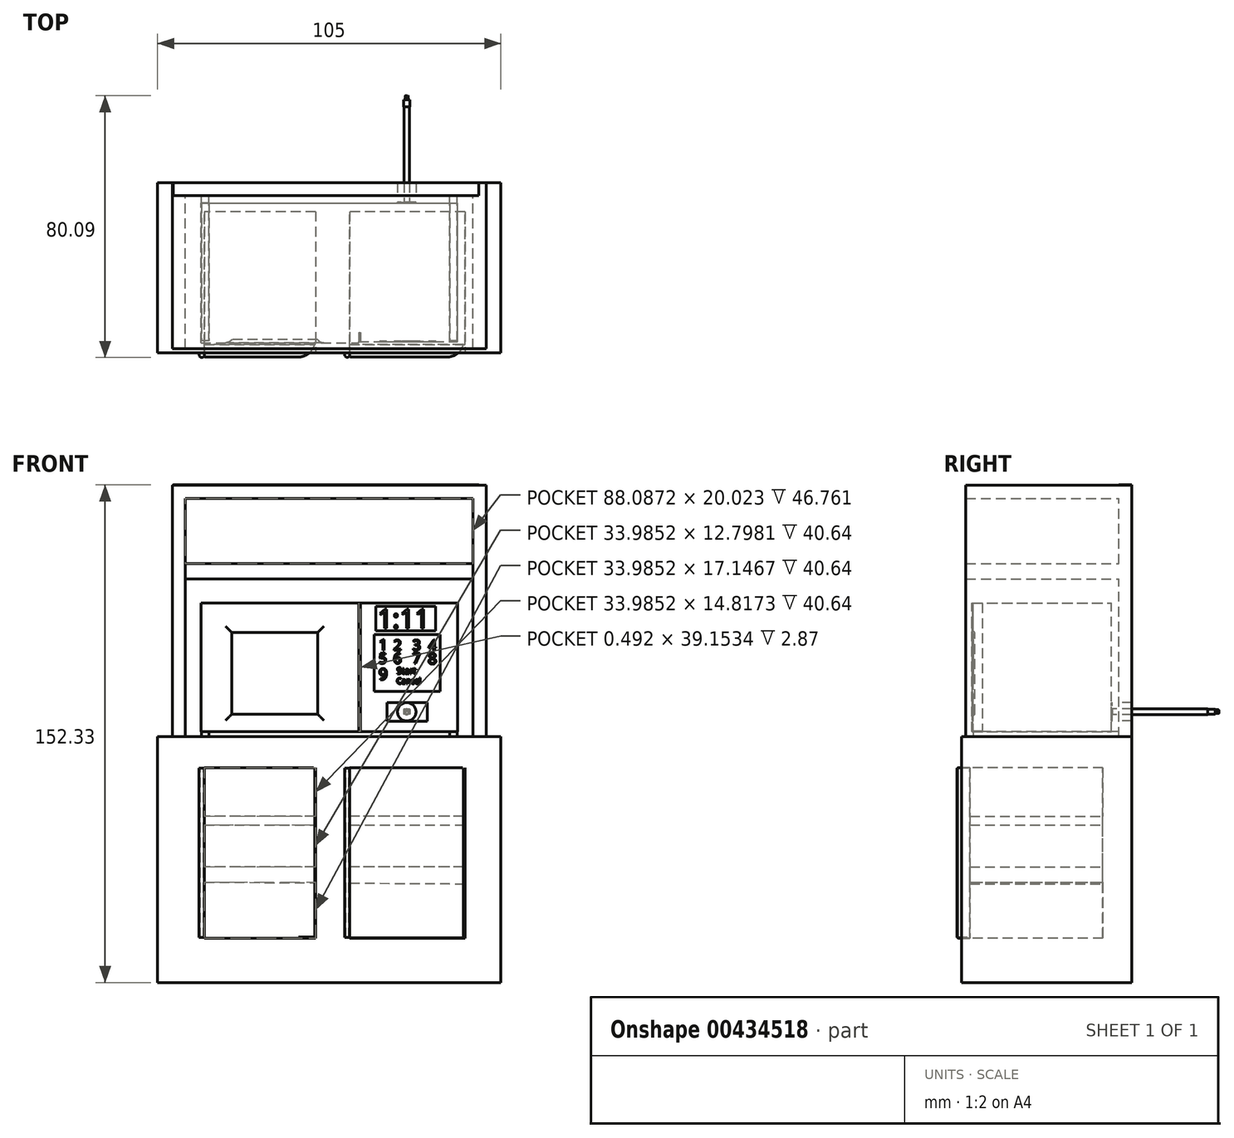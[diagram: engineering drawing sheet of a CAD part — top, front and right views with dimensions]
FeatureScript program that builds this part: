
annotation { "Feature Type Name" : "Feature", "Feature Type Description" : "" }
export const myFeature = defineFeature(function(context is Context, id is Id, definition is map)
    precondition{}
    {
        {
            var Q0;
            Q0=qCreatedBy(makeId("Front.planeOp"),FACE);
            var sketch = newSketch(context, id + "F0", { "sketchPlane" : qUnion([Q0])});
            skLineSegment(sketch, "E0", {"start": v(-38.7, 76.96) * mm, "end": v(57.3, 76.96) * mm});
            skLineSegment(sketch, "E1", {"start": v(57.3, 76.96) * mm, "end": v(57.3, 0) * mm});
            skLineSegment(sketch, "E2", {"start": v(53.34, 0) * mm, "end": v(53.34, 73) * mm});
            skLineSegment(sketch, "E3", {"start": v(53.34, 73) * mm, "end": v(-34.75, 73) * mm});
            skLineSegment(sketch, "E4", {"start": v(-34.75, 73) * mm, "end": v(-34.75, 0) * mm});
            skLineSegment(sketch, "E5", {"start": v(-38.7, 0) * mm, "end": v(-38.7, 76.96) * mm});
            skLineSegment(sketch, "E6", {"start": v(61.8, 0) * mm, "end": v(-43.2, 0) * mm});
            skLineSegment(sketch, "E7", {"start": v(-43.2, 0) * mm, "end": v(-43.2, -75.21) * mm});
            skLineSegment(sketch, "E8", {"start": v(-43.2, -75.21) * mm, "end": v(61.8, -75.21) * mm});
            skLineSegment(sketch, "E9", {"start": v(61.8, -75.21) * mm, "end": v(61.8, 0) * mm});
            skSolve(sketch);
        }
        {
            var Q0;
            Q0=makeQuery(id+"F0.imprint","IMPRINT",FACE,{"disambiguationData":[TD([[makeQuery(id+"F0.imprint","IMPRINT",EDGE,{"derivedFrom":sQuery(id+"F0.wireOp",EDGE,"E0")}),-1.0]])]});
            extrude(context, id + "F1", {"entities" : qUnion([Q0]), "depth" : 50.8 * mm});
        }
        {
            var Q0;
            {var subQ6=sQuery(id+"F0.wireOp",EDGE,"E7");Q0=makeQuery(id+"F0.imprint","IMPRINT",FACE,{"disambiguationData":[TD([[makeQuery(id+"F0.imprint","IMPRINT",EDGE,{"derivedFrom":subQ6}),1.0]])]});}
            extrude(context, id + "F2", {"entities" : qUnion([Q0]), "operationType" : NewBodyOperationType.ADD, "depth" : 52.07 * mm});
        }
        {
            var Q0;
            Q0=qCreatedBy(makeId("Right.planeOp"),FACE);
            var sketch = newSketch(context, id + "F3", { "sketchPlane" : qUnion([Q0])});
            skLineSegment(sketch, "E10", {"start": v(0, 77.12) * mm, "end": v(0, 0) * mm});
            skLineSegment(sketch, "E11", {"start": v(0, 0) * mm, "end": v(-3.98, 0) * mm});
            skLineSegment(sketch, "E12", {"start": v(-3.98, 0) * mm, "end": v(-3.98, 77.12) * mm});
            skLineSegment(sketch, "E13", {"start": v(-3.98, 77.12) * mm, "end": v(0, 77.12) * mm});
            skSolve(sketch);
        }
        {
            var Q0;
            Q0=makeQuery(id+"F3.imprint","IMPRINT",FACE,{"disambiguationData":[TD([[makeQuery(id+"F3.imprint","IMPRINT",EDGE,{"derivedFrom":sQuery(id+"F3.wireOp",EDGE,"E10")}),-1.0]])]});
            extrude(context, id + "F4", {"entities" : qUnion([Q0]), "operationType" : NewBodyOperationType.ADD, "depth" : 55.12 * mm});
        }
        {
            var Q0;
            Q0=makeQuery(id+"F3.imprint","IMPRINT",FACE,{"disambiguationData":[TD([[makeQuery(id+"F3.imprint","IMPRINT",EDGE,{"derivedFrom":sQuery(id+"F3.wireOp",EDGE,"E10")}),-1.0]])]});
            extrude(context, id + "F5", {"entities" : qUnion([Q0]), "operationType" : NewBodyOperationType.ADD, "oppositeDirection" : true, "depth" : 38.35 * mm});
        }
        {
            var Q0;
            Q0=makeQuery(id+"F2.opExtrude","CAP_FACE",FACE,{"disambiguationData":[OSD([sQuery(id+"F0.wireOp",EDGE,"E6"),sQuery(id+"F0.wireOp",EDGE,"E7"),sQuery(id+"F0.wireOp",EDGE,"E8"),sQuery(id+"F0.wireOp",EDGE,"E9")])],"isStart":false});
            var sketch = newSketch(context, id + "F6", { "sketchPlane" : qUnion([Q0])});
            skLineSegment(sketch, "E14", {"start": v(-28.82, -9.5) * mm, "end": v(-28.82, -61.64) * mm});
            skLineSegment(sketch, "E15", {"start": v(-28.82, -61.64) * mm, "end": v(5.16, -61.64) * mm});
            skLineSegment(sketch, "E16", {"start": v(5.16, -61.64) * mm, "end": v(5.16, -9.5) * mm});
            skLineSegment(sketch, "E17", {"start": v(5.16, -9.5) * mm, "end": v(-28.82, -9.5) * mm});
            skLineSegment(sketch, "E18", {"start": v(15.64, -9.5) * mm, "end": v(15.64, -61.64) * mm});
            skLineSegment(sketch, "E19", {"start": v(15.64, -61.64) * mm, "end": v(50.9, -61.64) * mm});
            skLineSegment(sketch, "E20", {"start": v(50.9, -61.64) * mm, "end": v(50.9, -9.5) * mm});
            skLineSegment(sketch, "E21", {"start": v(50.9, -9.5) * mm, "end": v(15.64, -9.5) * mm});
            skSolve(sketch);
        }
        {
            var Q0;
            Q0=makeQuery(id+"F6.imprint","IMPRINT",FACE,{"disambiguationData":[TD([[makeQuery(id+"F6.imprint","IMPRINT",EDGE,{"derivedFrom":sQuery(id+"F6.wireOp",EDGE,"E18")}),1.0]])]});
            var Q1;
            Q1=makeQuery(id+"F6.imprint","IMPRINT",FACE,{"disambiguationData":[TD([[makeQuery(id+"F6.imprint","IMPRINT",EDGE,{"derivedFrom":sQuery(id+"F6.wireOp",EDGE,"E14")}),1.0]])]});
            extrude(context, id + "F7", {"entities" : qUnion([Q0, Q1]), "operationType" : NewBodyOperationType.REMOVE, "oppositeDirection" : true, "depth" : 43.18 * mm});
        }
        {
            var Q0;
            Q0=makeQuery(id+"F7.boolean.opBoolean","COPY",FACE,{"derivedFrom":makeQuery(id+"F7.opExtrude","CAP_FACE",FACE,{"disambiguationData":[OSD([sQuery(id+"F6.wireOp",EDGE,"E14"),sQuery(id+"F6.wireOp",EDGE,"E15"),sQuery(id+"F6.wireOp",EDGE,"E16"),sQuery(id+"F6.wireOp",EDGE,"E17")])],"isStart":false})});
            var sketch = newSketch(context, id + "F8", { "sketchPlane" : qUnion([Q0])});
            skLineSegment(sketch, "E22", {"start": v(50.86, -24.33) * mm, "end": v(-28.82, -24.33) * mm});
            skLineSegment(sketch, "E23", {"start": v(-28.82, -24.33) * mm, "end": v(-28.82, -27) * mm});
            skLineSegment(sketch, "E24", {"start": v(-28.82, -27) * mm, "end": v(50.86, -27) * mm});
            skLineSegment(sketch, "E25", {"start": v(50.86, -27) * mm, "end": v(50.86, -24.33) * mm});
            skLineSegment(sketch, "E26", {"start": v(-28.82, -39.8) * mm, "end": v(-28.82, -44.49) * mm});
            skLineSegment(sketch, "E27", {"start": v(-28.82, -44.49) * mm, "end": v(50.86, -45) * mm});
            skLineSegment(sketch, "E28", {"start": v(50.86, -45) * mm, "end": v(50.86, -39.8) * mm});
            skLineSegment(sketch, "E29", {"start": v(50.86, -39.8) * mm, "end": v(-28.82, -39.8) * mm});
            skSolve(sketch);
        }
        {
            var Q0;
            {var subQ0=sQuery(id+"F8.wireOp",EDGE,"E28");Q0=makeQuery(id+"F8.imprint","IMPRINT",FACE,{"disambiguationData":[TD([[makeQuery(id+"F8.imprint","IMPRINT",EDGE,{"derivedFrom":subQ0}),1.0]])]});}
            var Q1;
            {var subQ0=sQuery(id+"F8.wireOp",EDGE,"E26");Q1=makeQuery(id+"F8.imprint","IMPRINT",FACE,{"disambiguationData":[TD([[makeQuery(id+"F8.imprint","IMPRINT",EDGE,{"derivedFrom":subQ0}),1.0]])]});}
            var Q2;
            {var subQ0=sQuery(id+"F8.wireOp",EDGE,"E25");Q2=makeQuery(id+"F8.imprint","IMPRINT",FACE,{"disambiguationData":[TD([[makeQuery(id+"F8.imprint","IMPRINT",EDGE,{"derivedFrom":subQ0}),1.0]])]});}
            var Q3;
            {var subQ0=sQuery(id+"F8.wireOp",EDGE,"E23");Q3=makeQuery(id+"F8.imprint","IMPRINT",FACE,{"disambiguationData":[TD([[makeQuery(id+"F8.imprint","IMPRINT",EDGE,{"derivedFrom":subQ0}),1.0]])]});}
            extrude(context, id + "F9", {"entities" : qUnion([Q0, Q1, Q2, Q3]), "operationType" : NewBodyOperationType.ADD, "depth" : 40.64 * mm});
        }
        {
            var Q0;
            {var subQ0=sQuery(id+"F3.wireOp",EDGE,"E12");Q0=makeQuery(id+"F5.boolean.opBoolean","MERGE",FACE,{"derivedFrom":[makeQuery(id+"F4.boolean.opBoolean","SPLIT",FACE,{"disambiguationData":[TD([makeQuery(id+"F1.opExtrude","SWEPT_FACE",FACE,{"disambiguationData":[OSD([sQuery(id+"F0.wireOp",EDGE,"E2")])]})])],"derivedFrom":makeQuery(id+"F4.opExtrude","SWEPT_FACE",FACE,{"disambiguationData":[OSD([subQ0])]})}),makeQuery(id+"F5.opExtrude","SWEPT_FACE",FACE,{"disambiguationData":[OSD([subQ0])]})]});}
            var sketch = newSketch(context, id + "F10", { "sketchPlane" : qUnion([Q0])});
            skCircle(sketch, "E30", {"center": v(33.06, 7.65) * mm, "radius": 2.83 * mm});
            skSolve(sketch);
        }
        {
            var Q0;
            Q0=makeQuery(id+"F10.imprint","IMPRINT",FACE,{"disambiguationData":[TD([[makeQuery(id+"F10.imprint","IMPRINT",EDGE,{"derivedFrom":sQuery(id+"F10.wireOp",EDGE,"efgbg2Ga-GxNY-wFfy-7I2s-iyKWtmELquTM")}),1.0]])]});
            var Q1;
            Q1=makeQuery(id+"F10.imprint","IMPRINT",FACE,{"disambiguationData":[TD([[makeQuery(id+"F10.imprint","IMPRINT",EDGE,{"derivedFrom":sQuery(id+"F10.wireOp",EDGE,"E30")}),1.0]])]});
            extrude(context, id + "F11", {"entities" : qUnion([Q0, Q1]), "operationType" : NewBodyOperationType.REMOVE, "oppositeDirection" : true, "depth" : 25.4 * mm});
        }
        {
            var Q0;
            {var subQ0=sQuery(id+"F3.wireOp",EDGE,"E12");Q0=makeQuery(id+"F5.boolean.opBoolean","MERGE",FACE,{"derivedFrom":[makeQuery(id+"F4.boolean.opBoolean","SPLIT",FACE,{"disambiguationData":[TD([makeQuery(id+"F1.opExtrude","SWEPT_FACE",FACE,{"disambiguationData":[OSD([sQuery(id+"F0.wireOp",EDGE,"E2")])]})])],"derivedFrom":makeQuery(id+"F4.opExtrude","SWEPT_FACE",FACE,{"disambiguationData":[OSD([subQ0])]})}),makeQuery(id+"F5.opExtrude","SWEPT_FACE",FACE,{"disambiguationData":[OSD([subQ0])]})]});}
            var sketch = newSketch(context, id + "F12", { "sketchPlane" : qUnion([Q0])});
            skLineSegment(sketch, "E31.bottom", {"start": v(-29.95, 1.61) * mm, "end": v(48.54, 1.61) * mm});
            skLineSegment(sketch, "E31.top", {"start": v(-29.95, 40.9) * mm, "end": v(48.54, 40.9) * mm});
            skLineSegment(sketch, "E31.left", {"start": v(-29.95, 1.61) * mm, "end": v(-29.95, 40.9) * mm});
            skLineSegment(sketch, "E31.right", {"start": v(48.54, 1.61) * mm, "end": v(48.54, 40.9) * mm});
            skSolve(sketch);
        }
        {
            var Q0;
            Q0=makeQuery(id+"F12.imprint","IMPRINT",FACE,{"disambiguationData":[TD([[makeQuery(id+"F12.imprint","IMPRINT",EDGE,{"derivedFrom":sQuery(id+"F12.wireOp",EDGE,"E31.bottom")}),1.0]])]});
            extrude(context, id + "F13", {"entities" : qUnion([Q0]), "operationType" : NewBodyOperationType.ADD, "depth" : 44.7 * mm, "hasSecondDirection" : true, "secondDirectionOppositeDirection" : false, "secondDirectionDepth" : 2.3 * mm});
        }
        {
            var Q0;
            Q0=makeQuery(id+"F13.opExtrude","CAP_FACE",FACE,{"disambiguationData":[OSD([sQuery(id+"F10.wireOp",EDGE,"E30"),sQuery(id+"F12.wireOp",EDGE,"E31.bottom"),sQuery(id+"F12.wireOp",EDGE,"E31.top"),sQuery(id+"F12.wireOp",EDGE,"E31.left"),sQuery(id+"F12.wireOp",EDGE,"E31.right")])],"isStart":false});
            var sketch = newSketch(context, id + "F14", { "sketchPlane" : qUnion([Q0])});
            skCircle(sketch, "E32", {"center": v(33.06, 7.65) * mm, "radius": 2.86 * mm});
            skSolve(sketch);
        }
        {
            var Q0;
            Q0=makeQuery(id+"F14.imprint","IMPRINT",FACE,{"disambiguationData":[TD([[makeQuery(id+"F14.imprint","IMPRINT",EDGE,{"derivedFrom":makeQuery(id+"F13.opExtrude","CAP_EDGE",EDGE,{"disambiguationData":[OSD([sQuery(id+"F10.wireOp",EDGE,"E30")])],"isStart":false})}),1.0]])]});
            extrude(context, id + "F15", {"entities" : qUnion([Q0]), "operationType" : NewBodyOperationType.ADD, "depth" : 0.08 * mm, "hasSecondDirection" : true, "secondDirectionOppositeDirection" : true, "secondDirectionDepth" : 42.72 * mm});
        }
        {
            var Q0;
            Q0=makeQuery(id+"F13.opExtrude","CAP_FACE",FACE,{"disambiguationData":[OSD([sQuery(id+"F10.wireOp",EDGE,"E30"),sQuery(id+"F12.wireOp",EDGE,"E31.bottom"),sQuery(id+"F12.wireOp",EDGE,"E31.top"),sQuery(id+"F12.wireOp",EDGE,"E31.left"),sQuery(id+"F12.wireOp",EDGE,"E31.right")])],"isStart":false});
            var sketch = newSketch(context, id + "F16", { "sketchPlane" : qUnion([Q0])});
            skLineSegment(sketch, "E33", {"start": v(18.4, 40.9) * mm, "end": v(18.4, 1.61) * mm});
            skLineSegment(sketch, "E34", {"start": v(18.4, 1.61) * mm, "end": v(-29.95, 1.61) * mm});
            skLineSegment(sketch, "E35", {"start": v(-29.95, 1.61) * mm, "end": v(-29.95, 40.9) * mm});
            skLineSegment(sketch, "E36", {"start": v(-29.95, 40.9) * mm, "end": v(18.4, 40.9) * mm});
            skLineSegment(sketch, "E37", {"start": v(18.89, 40.9) * mm, "end": v(18.89, 1.61) * mm});
            skLineSegment(sketch, "E38", {"start": v(18.4, 40.84) * mm, "end": v(18.89, 40.84) * mm});
            skLineSegment(sketch, "E39", {"start": v(18.4, 1.69) * mm, "end": v(18.89, 1.69) * mm});
            skLineSegment(sketch, "E40", {"start": v(5.75, 31.9) * mm, "end": v(-20.45, 31.9) * mm});
            skLineSegment(sketch, "E41", {"start": v(-20.45, 31.9) * mm, "end": v(-20.45, 6.96) * mm});
            skLineSegment(sketch, "E42", {"start": v(-20.45, 6.96) * mm, "end": v(5.75, 6.96) * mm});
            skLineSegment(sketch, "E43", {"start": v(5.75, 6.96) * mm, "end": v(5.75, 31.9) * mm});
            skSolve(sketch);
        }
        {
            var Q0;
            Q0=makeQuery(id+"F16.imprint","IMPRINT",FACE,{"disambiguationData":[TD([[makeQuery(id+"F16.imprint","IMPRINT",EDGE,{"derivedFrom":sQuery(id+"F16.wireOp",EDGE,"E33")}),-1.0]])]});
            extrude(context, id + "F17", {"entities" : qUnion([Q0]), "operationType" : NewBodyOperationType.ADD, "depth" : 0.3 * mm});
        }
        {
            var Q0;
            {var subQ0=sQuery(id+"F16.wireOp",EDGE,"E38");Q0=makeQuery(id+"F16.imprint","IMPRINT",FACE,{"disambiguationData":[TD([[makeQuery(id+"F16.imprint","IMPRINT",EDGE,{"derivedFrom":subQ0}),-1.0]])]});}
            extrude(context, id + "F18", {"entities" : qUnion([Q0]), "operationType" : NewBodyOperationType.REMOVE, "oppositeDirection" : true, "depth" : 2.87 * mm});
        }
        {
            var Q0;
            Q0=makeQuery(id+"F16.imprint","IMPRINT",FACE,{"disambiguationData":[TD([[makeQuery(id+"F16.imprint","IMPRINT",EDGE,{"derivedFrom":sQuery(id+"F16.wireOp",EDGE,"E40")}),1.0]])]});
            extrude(context, id + "F19", {"entities" : qUnion([Q0]), "operationType" : NewBodyOperationType.REMOVE, "oppositeDirection" : true, "depth" : 0.63 * mm});
        }
        {
            var Q0;
            Q0=makeQuery(id+"F17.opExtrude","CAP_EDGE",EDGE,{"disambiguationData":[OSD([sQuery(id+"F16.wireOp",EDGE,"E43")])],"isStart":false});
            var Q1;
            Q1=makeQuery(id+"F17.opExtrude","CAP_EDGE",EDGE,{"disambiguationData":[OSD([sQuery(id+"F16.wireOp",EDGE,"E40")])],"isStart":false});
            var Q2;
            Q2=makeQuery(id+"F17.opExtrude","CAP_EDGE",EDGE,{"disambiguationData":[OSD([sQuery(id+"F16.wireOp",EDGE,"E41")])],"isStart":false});
            var Q3;
            Q3=makeQuery(id+"F17.opExtrude","CAP_EDGE",EDGE,{"disambiguationData":[OSD([sQuery(id+"F16.wireOp",EDGE,"E42")])],"isStart":false});
            fillet(context, id + "F20", {"entities" : qUnion([Q0, Q1, Q2, Q3]), "radius" : 2.54 * mm, "tangentPropagation" : true, "allowEdgeOverflow" : false});
        }
        {
            var Q0;
            {var subQ0=sQuery(id+"F12.wireOp",EDGE,"E31.top");var subQ1=sQuery(id+"F10.wireOp",EDGE,"E30");var subQ2=sQuery(id+"F12.wireOp",EDGE,"E31.right");var subQ3=sQuery(id+"F12.wireOp",EDGE,"E31.bottom");Q0=makeQuery(id+"F17.boolean.opBoolean","SPLIT",FACE,{"disambiguationData":[TD([makeQuery(id+"F13.opExtrude","SWEPT_FACE",FACE,{"disambiguationData":[OSD([subQ3])]})])],"derivedFrom":makeQuery(id+"F13.opExtrude","CAP_FACE",FACE,{"disambiguationData":[OSD([subQ1,subQ3,subQ0,sQuery(id+"F12.wireOp",EDGE,"E31.left"),subQ2])],"isStart":false})});}
            var sketch = newSketch(context, id + "F21", { "sketchPlane" : qUnion([Q0])});
            skLineSegment(sketch, "E44.bottom", {"start": v(27, 10.53) * mm, "end": v(39.33, 10.53) * mm});
            skLineSegment(sketch, "E44.top", {"start": v(27, 4.79) * mm, "end": v(39.33, 4.79) * mm});
            skLineSegment(sketch, "E44.left", {"start": v(27, 10.53) * mm, "end": v(27, 4.79) * mm});
            skLineSegment(sketch, "E44.right", {"start": v(39.33, 10.53) * mm, "end": v(39.33, 4.79) * mm});
            skLineSegment(sketch, "E45.bottom", {"start": v(23.05, 31.25) * mm, "end": v(43.3, 31.25) * mm});
            skLineSegment(sketch, "E45.top", {"start": v(23.05, 13.91) * mm, "end": v(43.3, 13.91) * mm});
            skLineSegment(sketch, "E45.left", {"start": v(23.05, 31.25) * mm, "end": v(23.05, 13.91) * mm});
            skLineSegment(sketch, "E45.right", {"start": v(43.3, 31.25) * mm, "end": v(43.3, 13.91) * mm});
            skLineSegment(sketch, "E46.bottom", {"start": v(23.62, 39.88) * mm, "end": v(41.89, 39.88) * mm});
            skLineSegment(sketch, "E46.top", {"start": v(23.62, 32.47) * mm, "end": v(41.89, 32.47) * mm});
            skLineSegment(sketch, "E46.left", {"start": v(23.62, 39.88) * mm, "end": v(23.62, 32.47) * mm});
            skLineSegment(sketch, "E46.right", {"start": v(41.89, 39.88) * mm, "end": v(41.89, 32.47) * mm});
            skSolve(sketch);
        }
        {
            var Q0;
            Q0=makeQuery(id+"F21.imprint","IMPRINT",FACE,{"disambiguationData":[TD([[makeQuery(id+"F21.imprint","IMPRINT",EDGE,{"derivedFrom":sQuery(id+"F21.wireOp",EDGE,"E46.bottom")}),-1.0]])]});
            var Q1;
            Q1=makeQuery(id+"F21.imprint","IMPRINT",FACE,{"disambiguationData":[TD([[makeQuery(id+"F21.imprint","IMPRINT",EDGE,{"derivedFrom":sQuery(id+"F21.wireOp",EDGE,"E45.bottom")}),-1.0]])]});
            var Q2;
            Q2=makeQuery(id+"F21.imprint","IMPRINT",FACE,{"disambiguationData":[TD([[makeQuery(id+"F21.imprint","IMPRINT",EDGE,{"derivedFrom":sQuery(id+"F21.wireOp",EDGE,"E44.bottom")}),-1.0]])]});
            var Q3;
            Q3=makeQuery(id+"F15.opExtrude","CAP_FACE",FACE,{"disambiguationData":[OSD([sQuery(id+"F10.wireOp",EDGE,"E30")])],"isStart":false});
            extrude(context, id + "F22", {"entities" : qUnion([Q0, Q1, Q2, Q3]), "operationType" : NewBodyOperationType.REMOVE, "oppositeDirection" : true, "depth" : 0.05 * mm});
        }
        {
            var Q0;
            Q0=makeQuery(id+"F22.boolean.opBoolean","COPY",FACE,{"derivedFrom":makeQuery(id+"F22.opExtrude","CAP_FACE",FACE,{"disambiguationData":[OSD([sQuery(id+"F21.wireOp",EDGE,"E45.bottom"),sQuery(id+"F21.wireOp",EDGE,"E45.top"),sQuery(id+"F21.wireOp",EDGE,"E45.left"),sQuery(id+"F21.wireOp",EDGE,"E45.right")])],"isStart":false})});
            var sketch = newSketch(context, id + "F23", { "sketchPlane" : qUnion([Q0])});
            skText(sketch, "E47", { "text": "1", "fontName": "OpenSans-Regular.ttf"});
            skText(sketch, "E48", { "text": "2\n", "fontName": "OpenSans-Regular.ttf"});
            skText(sketch, "E49", { "text": "3", "fontName": "OpenSans-Regular.ttf"});
            skText(sketch, "E50", { "text": "4", "fontName": "OpenSans-Regular.ttf"});
            skText(sketch, "E51", { "text": "Start", "fontName": "OpenSans-Regular.ttf"});
            skText(sketch, "E52", { "text": "Cancel", "fontName": "OpenSans-Regular.ttf"});
            skText(sketch, "E53", { "text": "5\n", "fontName": "OpenSans-Regular.ttf"});
            skText(sketch, "E54", { "text": "6", "fontName": "OpenSans-Regular.ttf"});
            skText(sketch, "E55", { "text": "7", "fontName": "OpenSans-Regular.ttf"});
            skText(sketch, "E56", { "text": "8", "fontName": "OpenSans-Regular.ttf"});
            skText(sketch, "E57", { "text": "9", "fontName": "OpenSans-Regular.ttf"});
            const initialGuessF23  = {"E47": [0.02447, 0.02651, 1, 0, 0.00335], "E48": [0.02897, 0.02651, 1, 0, 0.00314], "E49": [0.03482, 0.0265, 1, 0, 0.00316], "E50": [0.03963, 0.0265, 1, 0, 0.00316], "E51": [0.03001, 0.01927, 1, 0, 0.00192], "E52": [0.02995, 0.01624, 1, 0, 0.00173], "E53": [0.02447, 0.02246, 1, 0, 0.00311], "E54": [0.02897, 0.02246, 1, 0, 0.00311], "E55": [0.03482, 0.02246, 1, 0, 0.00311], "E56": [0.03954, 0.02228, 1, 0, 0.00336], "E57": [0.02447, 0.0175, 1, 0, 0.0034]};
            skSetInitialGuess(sketch, initialGuessF23);
            skSolve(sketch);
        }
        {
            var Q0;
            Q0 = qSketchRegion(id + "F23", true);
            extrude(context, id + "F24", {"entities" : qUnion([Q0]), "operationType" : NewBodyOperationType.REMOVE, "oppositeDirection" : true, "depth" : 0.13 * mm});
        }
        {
            var Q0;
            Q0=makeQuery(id+"F15.opExtrude","CAP_FACE",FACE,{"disambiguationData":[OSD([sQuery(id+"F10.wireOp",EDGE,"E30")])],"isStart":true});
            var sketch = newSketch(context, id + "F25", { "sketchPlane" : qUnion([Q0])});
            skCircle(sketch, "E58", {"center": v(-33.06, 7.65) * mm, "radius": 0.85 * mm});
            skSolve(sketch);
        }
        {
            var Q0;
            Q0=makeQuery(id+"F25.imprint","IMPRINT",FACE,{"disambiguationData":[TD([[makeQuery(id+"F25.imprint","IMPRINT",EDGE,{"derivedFrom":sQuery(id+"F25.wireOp",EDGE,"E58")}),1.0]])]});
            extrude(context, id + "F26", {"entities" : qUnion([Q0]), "operationType" : NewBodyOperationType.ADD, "depth" : 29.2 * mm});
        }
        {
            var Q0;
            {var subQ0=sQuery(id+"F8.wireOp",EDGE,"E22");var subQ1=sQuery(id+"F8.wireOp",EDGE,"E24");Q0=makeQuery(id+"F9.boolean.opBoolean","SPLIT",FACE,{"disambiguationData":[TD([makeQuery(id+"F7.boolean.opBoolean","COPY",FACE,{"derivedFrom":makeQuery(id+"F7.opExtrude","SWEPT_FACE",FACE,{"disambiguationData":[OSD([sQuery(id+"F6.wireOp",EDGE,"E14")])]})})])],"derivedFrom":makeQuery(id+"F9.opExtrude","CAP_FACE",FACE,{"disambiguationData":[OSD([subQ0,sQuery(id+"F8.wireOp",EDGE,"E23"),subQ1,sQuery(id+"F8.wireOp",EDGE,"E25")])],"isStart":false})});}
            var sketch = newSketch(context, id + "F27", { "sketchPlane" : qUnion([Q0])});
            skLineSegment(sketch, "E59", {"start": v(10.5, 0) * mm, "end": v(10.5, -75.45) * mm});
            skLineSegment(sketch, "E60", {"start": v(-28.82, -9.5) * mm, "end": v(-28.82, -61.63) * mm});
            skLineSegment(sketch, "E61", {"start": v(-28.82, -61.63) * mm, "end": v(-28.82, -61.63) * mm});
            skLineSegment(sketch, "E62", {"start": v(-28.82, -9.5) * mm, "end": v(4.86, -9.5) * mm});
            skLineSegment(sketch, "E63", {"start": v(4.86, -9.5) * mm, "end": v(4.86, -61.6) * mm});
            skLineSegment(sketch, "E64", {"start": v(4.86, -61.6) * mm, "end": v(-28.82, -61.63) * mm});
            skLineSegment(sketch, "E65", {"start": v(15.64, -9.5) * mm, "end": v(15.64, -61.6) * mm});
            skLineSegment(sketch, "E66", {"start": v(15.64, -61.6) * mm, "end": v(50.38, -61.6) * mm});
            skLineSegment(sketch, "E67", {"start": v(50.38, -61.6) * mm, "end": v(50.38, -9.5) * mm});
            skLineSegment(sketch, "E68", {"start": v(50.38, -9.5) * mm, "end": v(15.64, -9.5) * mm});
            skSolve(sketch);
        }
        {
            var Q0;
            {var subQ4=sQuery(id+"F27.wireOp",EDGE,"E64");Q0=makeQuery(id+"F27.imprint","IMPRINT",FACE,{"disambiguationData":[TD([[makeQuery(id+"F27.imprint","IMPRINT",EDGE,{"derivedFrom":subQ4}),-1.0]])]});}
            var Q1;
            {var subQ4=sQuery(id+"F27.wireOp",EDGE,"E62");Q1=makeQuery(id+"F27.imprint","IMPRINT",FACE,{"disambiguationData":[TD([[makeQuery(id+"F27.imprint","IMPRINT",EDGE,{"derivedFrom":subQ4}),-1.0]])]});}
            var Q2;
            {var subQ0=sQuery(id+"F27.wireOp",EDGE,"E60");var subQ1=makeQuery(id+"F7.boolean.opBoolean","COPY",FACE,{"derivedFrom":makeQuery(id+"F7.opExtrude","SWEPT_FACE",FACE,{"disambiguationData":[OSD([sQuery(id+"F6.wireOp",EDGE,"E14")])]})});var subQ3=sQuery(id+"F8.wireOp",EDGE,"E22");var subQ6=makeQuery(id+"F9.boolean.opBoolean","SPLIT",EDGE,{"disambiguationData":[TD([subQ1])],"derivedFrom":makeQuery(id+"F9.opExtrude","CAP_EDGE",EDGE,{"disambiguationData":[OSD([subQ3])],"isStart":false})});var subQ7=makeQuery(id+"F27.imprint","INTERSECT",VERTEX,{"derivedFrom":[subQ6,subQ0]});Q2=makeQuery(id+"F27.imprint","IMPRINT",FACE,{"disambiguationData":[TD([[makeQuery(id+"F27.imprint","IMPRINT",EDGE,{"disambiguationData":[TD([[subQ7,-1.0]])],"derivedFrom":subQ0}),1.0]])]});}
            extrude(context, id + "F28", {"entities" : qUnion([Q0, Q1, Q2]), "depth" : 3.8 * mm});
        }
        {
            var Q0;
            Q0=makeQuery(id+"F27.imprint","IMPRINT",FACE,{"disambiguationData":[TD([[makeQuery(id+"F27.imprint","IMPRINT",EDGE,{"derivedFrom":sQuery(id+"F27.wireOp",EDGE,"E65")}),1.0]])]});
            extrude(context, id + "F29", {"entities" : qUnion([Q0]), "depth" : 3.8 * mm});
        }
        {
            var Q0;
            Q0=makeQuery(id+"F28.opExtrude","CAP_EDGE",EDGE,{"disambiguationData":[OSD([sQuery(id+"F27.wireOp",EDGE,"E63")])],"isStart":false});
            var Q1;
            Q1=makeQuery(id+"F29.opExtrude","CAP_EDGE",EDGE,{"disambiguationData":[OSD([sQuery(id+"F27.wireOp",EDGE,"E67")])],"isStart":false});
            fillet(context, id + "F30", {"entities" : qUnion([Q0, Q1]), "radius" : 5.08 * mm, "tangentPropagation" : true, "allowEdgeOverflow" : false});
        }
        {
            var Q0;
            Q0=makeQuery(id+"F29.opExtrude","CAP_EDGE",EDGE,{"disambiguationData":[OSD([sQuery(id+"F27.wireOp",EDGE,"E68")])],"isStart":false});
            var Q1;
            Q1=makeQuery(id+"F28.opExtrude","CAP_EDGE",EDGE,{"disambiguationData":[OSD([sQuery(id+"F27.wireOp",EDGE,"E62")])],"isStart":false});
            var Q2;
            Q2=makeQuery(id+"F29.opExtrude","CAP_FACE",FACE,{"disambiguationData":[OSD([sQuery(id+"F27.wireOp",EDGE,"E65"),sQuery(id+"F27.wireOp",EDGE,"E66"),sQuery(id+"F27.wireOp",EDGE,"E67"),sQuery(id+"F27.wireOp",EDGE,"E68")])],"isStart":false});
            var Q3;
            Q3=makeQuery(id+"F28.opExtrude","CAP_EDGE",EDGE,{"disambiguationData":[OSD([sQuery(id+"F27.wireOp",EDGE,"E60")])],"isStart":false});
            var Q4;
            Q4=makeQuery(id+"F28.opExtrude","CAP_EDGE",EDGE,{"disambiguationData":[OSD([sQuery(id+"F27.wireOp",EDGE,"E64")])],"isStart":false});
            fillet(context, id + "F31", {"entities" : qUnion([Q0, Q1, Q2, Q3, Q4]), "radius" : 0.25 * mm, "tangentPropagation" : true, "allowEdgeOverflow" : false});
        }
        {
            var Q0;
            Q0=makeQuery(id+"F22.boolean.opBoolean","COPY",FACE,{"derivedFrom":makeQuery(id+"F22.opExtrude","CAP_FACE",FACE,{"disambiguationData":[OSD([sQuery(id+"F21.wireOp",EDGE,"E46.bottom"),sQuery(id+"F21.wireOp",EDGE,"E46.top"),sQuery(id+"F21.wireOp",EDGE,"E46.left"),sQuery(id+"F21.wireOp",EDGE,"E46.right")])],"isStart":false})});
            var sketch = newSketch(context, id + "F32", { "sketchPlane" : qUnion([Q0])});
            skText(sketch, "E69", { "text": "1:11", "fontName": "OpenSans-Regular.ttf"});
            const initialGuessF32  = {"E69": [0.02407, 0.03325, 1, 0, 0.0058]};
            skSetInitialGuess(sketch, initialGuessF32);
            skSolve(sketch);
        }
        {
            var Q0;
            Q0 = qSketchRegion(id + "F32", true);
            extrude(context, id + "F33", {"entities" : qUnion([Q0]), "operationType" : NewBodyOperationType.ADD, "depth" : 0.08 * mm});
        }
        {
            var Q0;
            Q0=qCreatedBy(makeId("Top.planeOp"),FACE);
            var sketch = newSketch(context, id + "F34", { "sketchPlane" : qUnion([Q0])});
            skCircle(sketch, "E70", {"center": v(-29.66, -52.69) * mm, "radius": 0.8 * mm});
            skCircle(sketch, "E71", {"center": v(14.83, -52.69) * mm, "radius": 0.76 * mm});
            skSolve(sketch);
        }
        {
            var Q0;
            Q0=makeQuery(id+"F34.imprint","IMPRINT",FACE,{"disambiguationData":[TD([[makeQuery(id+"F34.imprint","IMPRINT",EDGE,{"derivedFrom":sQuery(id+"F34.wireOp",EDGE,"E70")}),1.0]])]});
            var Q1;
            Q1=makeQuery(id+"F34.imprint","IMPRINT",FACE,{"disambiguationData":[TD([[makeQuery(id+"F34.imprint","IMPRINT",EDGE,{"derivedFrom":sQuery(id+"F34.wireOp",EDGE,"E71")}),1.0]])]});
            extrude(context, id + "F35", {"entities" : qUnion([Q0, Q1]), "operationType" : NewBodyOperationType.ADD, "oppositeDirection" : true, "depth" : 61.47 * mm, "hasSecondDirection" : true, "secondDirectionOppositeDirection" : true, "secondDirectionDepth" : 9.65 * mm});
        }
        {
            var Q0;
            Q0=makeQuery(id+"F26.opExtrude","CAP_FACE",FACE,{"disambiguationData":[OSD([sQuery(id+"F25.wireOp",EDGE,"E58")])],"isStart":false});
            var sketch = newSketch(context, id + "F36", { "sketchPlane" : qUnion([Q0])});
            skLineSegment(sketch, "E72.bottom", {"start": v(-34.05, 8.38) * mm, "end": v(-32.07, 8.38) * mm});
            skLineSegment(sketch, "E72.top", {"start": v(-34.05, 6.93) * mm, "end": v(-32.07, 6.93) * mm});
            skLineSegment(sketch, "E72.left", {"start": v(-34.05, 8.38) * mm, "end": v(-34.05, 6.93) * mm});
            skLineSegment(sketch, "E72.right", {"start": v(-32.07, 8.38) * mm, "end": v(-32.07, 6.93) * mm});
            skSolve(sketch);
        }
        {
            var Q0;
            {var subQ0=sQuery(id+"F36.wireOp",EDGE,"E72.right");Q0=makeQuery(id+"F36.imprint","IMPRINT",FACE,{"disambiguationData":[TD([[makeQuery(id+"F36.imprint","IMPRINT",EDGE,{"derivedFrom":subQ0}),-1.0]])]});}
            var Q1;
            {var subQ0=sQuery(id+"F36.wireOp",EDGE,"E72.bottom");var subQ1=makeQuery(id+"F26.opExtrude","CAP_EDGE",EDGE,{"disambiguationData":[OSD([sQuery(id+"F25.wireOp",EDGE,"E58")])],"isStart":false});var subQ2=makeQuery(id+"F36.imprint","INTERSECT",VERTEX,{"disambiguationData":[OD(0.0)],"derivedFrom":[subQ1,subQ0]});Q1=makeQuery(id+"F36.imprint","IMPRINT",FACE,{"disambiguationData":[TD([[makeQuery(id+"F36.imprint","IMPRINT",EDGE,{"disambiguationData":[TD([[subQ2,-1.0]])],"derivedFrom":subQ0}),-1.0]])]});}
            var Q2;
            {var subQ0=sQuery(id+"F36.wireOp",EDGE,"E72.left");Q2=makeQuery(id+"F36.imprint","IMPRINT",FACE,{"disambiguationData":[TD([[makeQuery(id+"F36.imprint","IMPRINT",EDGE,{"derivedFrom":subQ0}),1.0]])]});}
            extrude(context, id + "F37", {"entities" : qUnion([Q0, Q1, Q2]), "operationType" : NewBodyOperationType.ADD, "depth" : 2.18 * mm});
        }
        {
            var Q0;
            Q0=makeQuery(id+"F37.opExtrude","CAP_FACE",FACE,{"disambiguationData":[OSD([sQuery(id+"F36.wireOp",EDGE,"E72.bottom"),sQuery(id+"F36.wireOp",EDGE,"E72.top"),sQuery(id+"F36.wireOp",EDGE,"E72.left"),sQuery(id+"F36.wireOp",EDGE,"E72.right")])],"isStart":false});
            var sketch = newSketch(context, id + "F38", { "sketchPlane" : qUnion([Q0])});
            skCircle(sketch, "E73", {"center": v(-33.06, 8.1) * mm, "radius": 0.17 * mm});
            skLineSegment(sketch, "E74.bottom", {"start": v(-33.55, 7.9) * mm, "end": v(-33.42, 7.9) * mm});
            skLineSegment(sketch, "E74.top", {"start": v(-33.55, 7.1) * mm, "end": v(-33.42, 7.1) * mm});
            skLineSegment(sketch, "E74.left", {"start": v(-33.55, 7.9) * mm, "end": v(-33.55, 7.1) * mm});
            skLineSegment(sketch, "E74.right", {"start": v(-33.42, 7.9) * mm, "end": v(-33.42, 7.1) * mm});
            skLineSegment(sketch, "E75.bottom", {"start": v(-32.7, 7.9) * mm, "end": v(-32.57, 7.9) * mm});
            skLineSegment(sketch, "E75.top", {"start": v(-32.7, 7.1) * mm, "end": v(-32.57, 7.1) * mm});
            skLineSegment(sketch, "E75.left", {"start": v(-32.7, 7.9) * mm, "end": v(-32.7, 7.1) * mm});
            skLineSegment(sketch, "E75.right", {"start": v(-32.57, 7.9) * mm, "end": v(-32.57, 7.1) * mm});
            skSolve(sketch);
        }
        {
            var Q0;
            Q0=makeQuery(id+"F38.imprint","IMPRINT",FACE,{"disambiguationData":[TD([[makeQuery(id+"F38.imprint","IMPRINT",EDGE,{"derivedFrom":sQuery(id+"F38.wireOp",EDGE,"E73")}),1.0]])]});
            var Q1;
            Q1=makeQuery(id+"F38.imprint","IMPRINT",FACE,{"disambiguationData":[TD([[makeQuery(id+"F38.imprint","IMPRINT",EDGE,{"derivedFrom":sQuery(id+"F38.wireOp",EDGE,"E75.bottom")}),-1.0]])]});
            var Q2;
            Q2=makeQuery(id+"F38.imprint","IMPRINT",FACE,{"disambiguationData":[TD([[makeQuery(id+"F38.imprint","IMPRINT",EDGE,{"derivedFrom":sQuery(id+"F38.wireOp",EDGE,"E74.bottom")}),-1.0]])]});
            extrude(context, id + "F39", {"entities" : qUnion([Q0, Q1, Q2]), "operationType" : NewBodyOperationType.ADD, "depth" : 1.17 * mm});
        }
        {
            var Q0;
            Q0=makeQuery(id+"F39.opExtrude","CAP_EDGE",EDGE,{"disambiguationData":[OSD([sQuery(id+"F38.wireOp",EDGE,"E73")])],"isStart":false});
            fillet(context, id + "F40", {"entities" : qUnion([Q0]), "radius" : 0.13 * mm, "tangentPropagation" : true, "allowEdgeOverflow" : false});
        }
        {
            var Q0;
            Q0=makeQuery(id+"F39.opExtrude","CAP_EDGE",EDGE,{"disambiguationData":[OSD([sQuery(id+"F38.wireOp",EDGE,"E74.right")])],"isStart":false});
            var Q1;
            Q1=makeQuery(id+"F39.opExtrude","CAP_EDGE",EDGE,{"disambiguationData":[OSD([sQuery(id+"F38.wireOp",EDGE,"E74.left")])],"isStart":false});
            var Q2;
            Q2=makeQuery(id+"F39.opExtrude","CAP_EDGE",EDGE,{"disambiguationData":[OSD([sQuery(id+"F38.wireOp",EDGE,"E74.top")])],"isStart":false});
            var Q3;
            Q3=makeQuery(id+"F39.opExtrude","CAP_EDGE",EDGE,{"disambiguationData":[OSD([sQuery(id+"F38.wireOp",EDGE,"E74.bottom")])],"isStart":false});
            var Q4;
            Q4=makeQuery(id+"F39.opExtrude","CAP_EDGE",EDGE,{"disambiguationData":[OSD([sQuery(id+"F38.wireOp",EDGE,"E75.bottom")])],"isStart":false});
            var Q5;
            Q5=makeQuery(id+"F39.opExtrude","CAP_EDGE",EDGE,{"disambiguationData":[OSD([sQuery(id+"F38.wireOp",EDGE,"E75.left")])],"isStart":false});
            var Q6;
            Q6=makeQuery(id+"F39.opExtrude","CAP_EDGE",EDGE,{"disambiguationData":[OSD([sQuery(id+"F38.wireOp",EDGE,"E75.top")])],"isStart":false});
            var Q7;
            Q7=makeQuery(id+"F39.opExtrude","CAP_EDGE",EDGE,{"disambiguationData":[OSD([sQuery(id+"F38.wireOp",EDGE,"E75.right")])],"isStart":false});
            fillet(context, id + "F41", {"entities" : qUnion([Q0, Q1, Q2, Q3, Q4, Q5, Q6, Q7]), "radius" : 0.03 * mm, "tangentPropagation" : true, "allowEdgeOverflow" : false});
        }
        {
            var Q0;
            {var subQ0=sQuery(id+"F3.wireOp",EDGE,"E12");Q0=makeQuery(id+"F5.boolean.opBoolean","MERGE",FACE,{"derivedFrom":[makeQuery(id+"F4.boolean.opBoolean","SPLIT",FACE,{"disambiguationData":[TD([makeQuery(id+"F1.opExtrude","SWEPT_FACE",FACE,{"disambiguationData":[OSD([sQuery(id+"F0.wireOp",EDGE,"E2")])]})])],"derivedFrom":makeQuery(id+"F4.opExtrude","SWEPT_FACE",FACE,{"disambiguationData":[OSD([subQ0])]})}),makeQuery(id+"F5.opExtrude","SWEPT_FACE",FACE,{"disambiguationData":[OSD([subQ0])]})]});}
            var sketch = newSketch(context, id + "F42", { "sketchPlane" : qUnion([Q0])});
            skLineSegment(sketch, "E76.bottom", {"start": v(-29.74, 0) * mm, "end": v(-27.48, 0) * mm});
            skLineSegment(sketch, "E76.top", {"start": v(-29.74, 1.74) * mm, "end": v(-27.48, 1.74) * mm});
            skLineSegment(sketch, "E76.left", {"start": v(-29.74, 0) * mm, "end": v(-29.74, 1.74) * mm});
            skLineSegment(sketch, "E76.right", {"start": v(-27.48, 0) * mm, "end": v(-27.48, 1.74) * mm});
            skLineSegment(sketch, "E77.bottom", {"start": v(48.41, 0) * mm, "end": v(46.16, 0) * mm});
            skLineSegment(sketch, "E77.top", {"start": v(48.41, 1.76) * mm, "end": v(46.16, 1.76) * mm});
            skLineSegment(sketch, "E77.left", {"start": v(48.41, 0) * mm, "end": v(48.41, 1.76) * mm});
            skLineSegment(sketch, "E77.right", {"start": v(46.16, 0) * mm, "end": v(46.16, 1.76) * mm});
            skSolve(sketch);
        }
        {
            var Q0;
            Q0=makeQuery(id+"F42.imprint","IMPRINT",FACE,{"disambiguationData":[TD([[makeQuery(id+"F42.imprint","IMPRINT",EDGE,{"derivedFrom":sQuery(id+"F42.wireOp",EDGE,"E76.bottom")}),-1.0]])]});
            var Q1;
            Q1=makeQuery(id+"F42.imprint","IMPRINT",FACE,{"disambiguationData":[TD([[makeQuery(id+"F42.imprint","IMPRINT",EDGE,{"derivedFrom":sQuery(id+"F42.wireOp",EDGE,"E77.bottom")}),-1.0]])]});
            extrude(context, id + "F43", {"entities" : qUnion([Q0, Q1]), "operationType" : NewBodyOperationType.ADD, "depth" : 44.45 * mm});
        }
        {
            var Q0;
            {var subQ0=sQuery(id+"F3.wireOp",EDGE,"E12");Q0=makeQuery(id+"F5.boolean.opBoolean","MERGE",FACE,{"derivedFrom":[makeQuery(id+"F4.boolean.opBoolean","SPLIT",FACE,{"disambiguationData":[TD([makeQuery(id+"F1.opExtrude","SWEPT_FACE",FACE,{"disambiguationData":[OSD([sQuery(id+"F0.wireOp",EDGE,"E2")])]})])],"derivedFrom":makeQuery(id+"F4.opExtrude","SWEPT_FACE",FACE,{"disambiguationData":[OSD([subQ0])]})}),makeQuery(id+"F5.opExtrude","SWEPT_FACE",FACE,{"disambiguationData":[OSD([subQ0])]})]});}
            var sketch = newSketch(context, id + "F44", { "sketchPlane" : qUnion([Q0])});
            skLineSegment(sketch, "E78.bottom", {"start": v(-34.75, 52.98) * mm, "end": v(53.34, 52.98) * mm});
            skLineSegment(sketch, "E78.top", {"start": v(-34.75, 48.26) * mm, "end": v(53.34, 48.26) * mm});
            skLineSegment(sketch, "E78.left", {"start": v(-34.75, 52.98) * mm, "end": v(-34.75, 48.26) * mm});
            skLineSegment(sketch, "E78.right", {"start": v(53.34, 52.98) * mm, "end": v(53.34, 48.26) * mm});
            skSolve(sketch);
        }
        {
            var Q0;
            Q0=makeQuery(id+"F44.imprint","IMPRINT",FACE,{"disambiguationData":[TD([[makeQuery(id+"F44.imprint","IMPRINT",EDGE,{"derivedFrom":sQuery(id+"F44.wireOp",EDGE,"E78.bottom")}),-1.0]])]});
            extrude(context, id + "F45", {"entities" : qUnion([Q0]), "operationType" : NewBodyOperationType.ADD, "depth" : 46.76 * mm});
        }
    });
